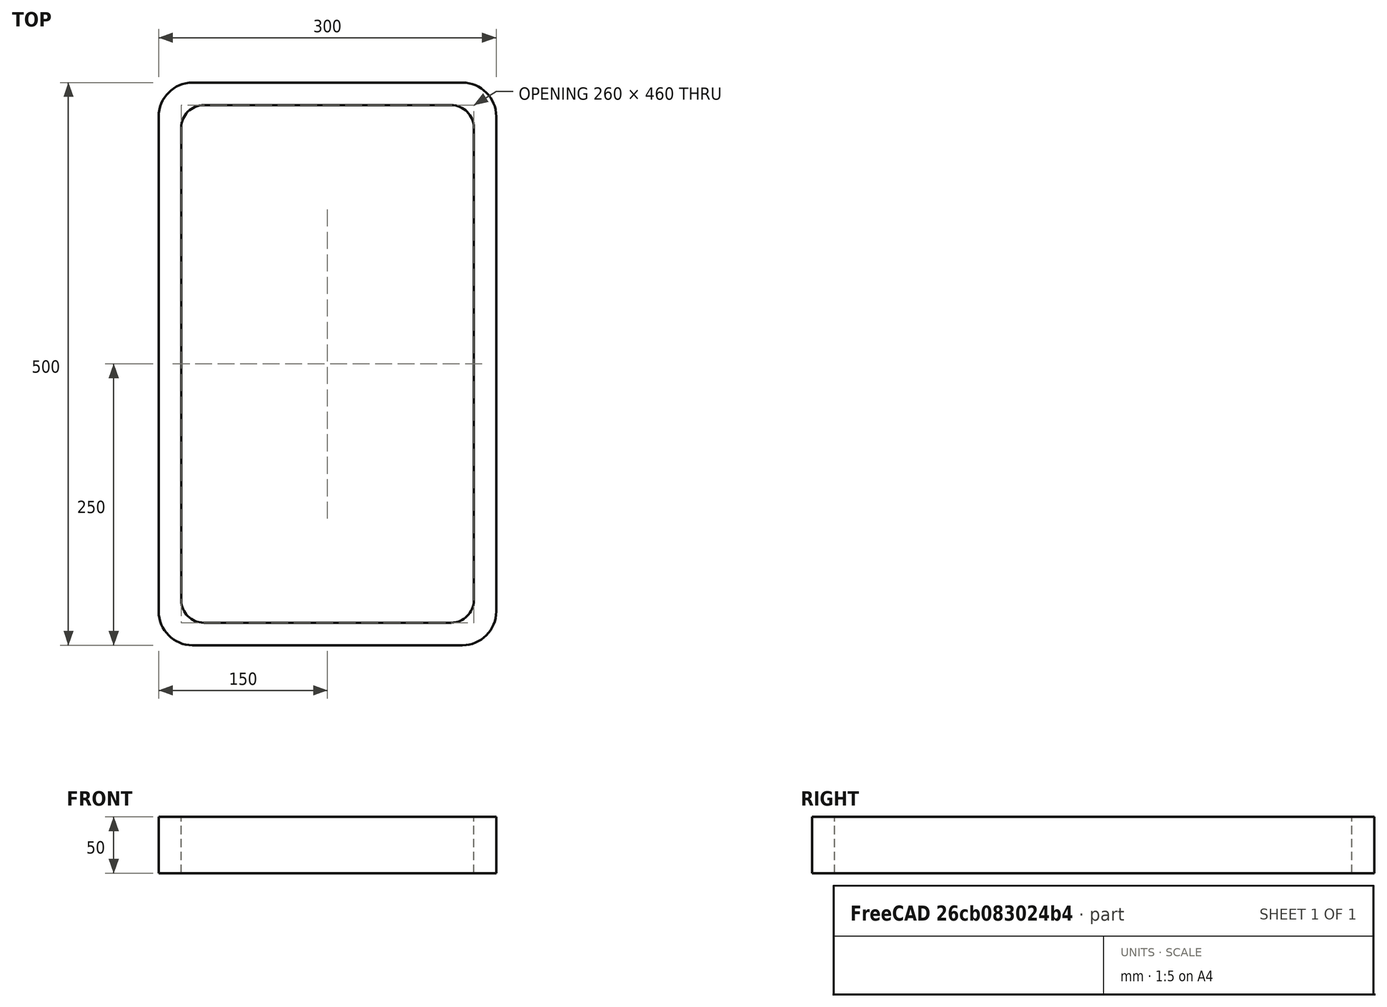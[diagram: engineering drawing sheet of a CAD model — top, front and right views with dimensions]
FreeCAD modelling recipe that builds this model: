
FCSTD DOCUMENT  (FreeCAD 0.15R4671 (Git))
Label: Rectangular hollow section 500x300x20 EN10219 S235JRH
License: All rights reserved
LicenseURL: http://en.wikipedia.org/wiki/All_rights_reserved
objects: Sketcher::SketchObject×1, Part::Extrusion×1
note: 2 computed .brp shape members not serialized (recipe doc carries the construction recipe); baked Part::Feature solids carry a one-line shape summary decoded from their .brp

FEATURE [Sketcher::SketchObject] Sketch
  sketch-geometry (16):
    g0: LineSegment StartX=-110 StartY=230 StartZ=0 EndX=110 EndY=230 EndZ=0
    g1: LineSegment StartX=130 StartY=210 StartZ=0 EndX=130 EndY=-210 EndZ=0
    g2: LineSegment StartX=110 StartY=-230 StartZ=0 EndX=-110 EndY=-230 EndZ=0
    g3: LineSegment StartX=-130 StartY=-210 StartZ=0 EndX=-130 EndY=210 EndZ=0
    g4: LineSegment StartX=-120 StartY=250 StartZ=0 EndX=120 EndY=250 EndZ=0
    g5: LineSegment StartX=150 StartY=220 StartZ=0 EndX=150 EndY=-220 EndZ=0
    g6: LineSegment StartX=120 StartY=-250 StartZ=0 EndX=-120 EndY=-250 EndZ=0
    g7: LineSegment StartX=-150 StartY=-220 StartZ=0 EndX=-150 EndY=220 EndZ=0
    g8: ArcOfCircle CenterX=-110 CenterY=210 CenterZ=0 NormalX=0 NormalY=0 NormalZ=1 Radius=20 StartAngle=1.5708 EndAngle=3.14159
    g9: ArcOfCircle CenterX=110 CenterY=210 CenterZ=0 NormalX=0 NormalY=0 NormalZ=1 Radius=20 StartAngle=0 EndAngle=1.5708
    g10: ArcOfCircle CenterX=110 CenterY=-210 CenterZ=0 NormalX=0 NormalY=0 NormalZ=1 Radius=20 StartAngle=4.71239 EndAngle=6.28319
    g11: ArcOfCircle CenterX=-110 CenterY=-210 CenterZ=0 NormalX=0 NormalY=0 NormalZ=1 Radius=20 StartAngle=3.14159 EndAngle=4.71239
    g12: ArcOfCircle CenterX=120 CenterY=220 CenterZ=0 NormalX=0 NormalY=0 NormalZ=1 Radius=30 StartAngle=0 EndAngle=1.5708
    g13: ArcOfCircle CenterX=120 CenterY=-220 CenterZ=0 NormalX=0 NormalY=0 NormalZ=1 Radius=30 StartAngle=4.71239 EndAngle=6.28319
    g14: ArcOfCircle CenterX=-120 CenterY=-220 CenterZ=0 NormalX=0 NormalY=0 NormalZ=1 Radius=30 StartAngle=3.14159 EndAngle=4.71239
    g15: ArcOfCircle CenterX=-120 CenterY=220 CenterZ=0 NormalX=0 NormalY=0 NormalZ=1 Radius=30 StartAngle=1.5708 EndAngle=3.14159
  constraints (36):
    c: Horizontal(g2)
    c: Vertical(g3)
    c: Horizontal(g6)
    c: Vertical(g7)
    c: Tangent(g3,g8) = 1.5708
    c: Tangent(g0,g8) = 1.5708
    c: Tangent(g0,g9) = 1.5708
    c: Tangent(g1,g9) = 1.5708
    c: Tangent(g1,g10) = 1.5708
    c: Tangent(g2,g10) = 1.5708
    c: Tangent(g2,g11) = 1.5708
    c: Tangent(g3,g11) = 1.5708
    c: Tangent(g4,g12) = 1.5708
    c: Tangent(g5,g12) = 1.5708
    c: Tangent(g5,g13) = 1.5708
    c: Tangent(g6,g13) = 1.5708
    c: Tangent(g6,g14) = 1.5708
    c: Tangent(g7,g14) = 1.5708
    c: Tangent(g7,g15) = 1.5708
    c: Tangent(g4,g15) = 1.5708
    c: Equal(g9,g8)
    c: Equal(g9,g11)
    c: Equal(g9,g10)
    c: Equal(g12,g15)
    c: Equal(g12,g14)
    c: Equal(g12,g13)
    c: Symmetric(g4,g6,g-1)
    c: Symmetric(g7,g5,g-2)
    c: DistanceY(g4,g6) = -500
    c: DistanceX(g7,g5) = 300
    c: Symmetric(g3,g1,g-2)
    c: Symmetric(g0,g2,g-1)
    c: DistanceY(g0,g4) = 20
    c: DistanceX(g5,g1) = -20
    c: Radius(g9) = 20
    c: Radius(g12) = 30
FEATURE [Part::Extrusion] Extrude  label="Rectangular hollow section 500x300x20 EN10219 S235JRH"
  Base = -> Sketch
  Dir = (0,0,50)
  Solid = true
